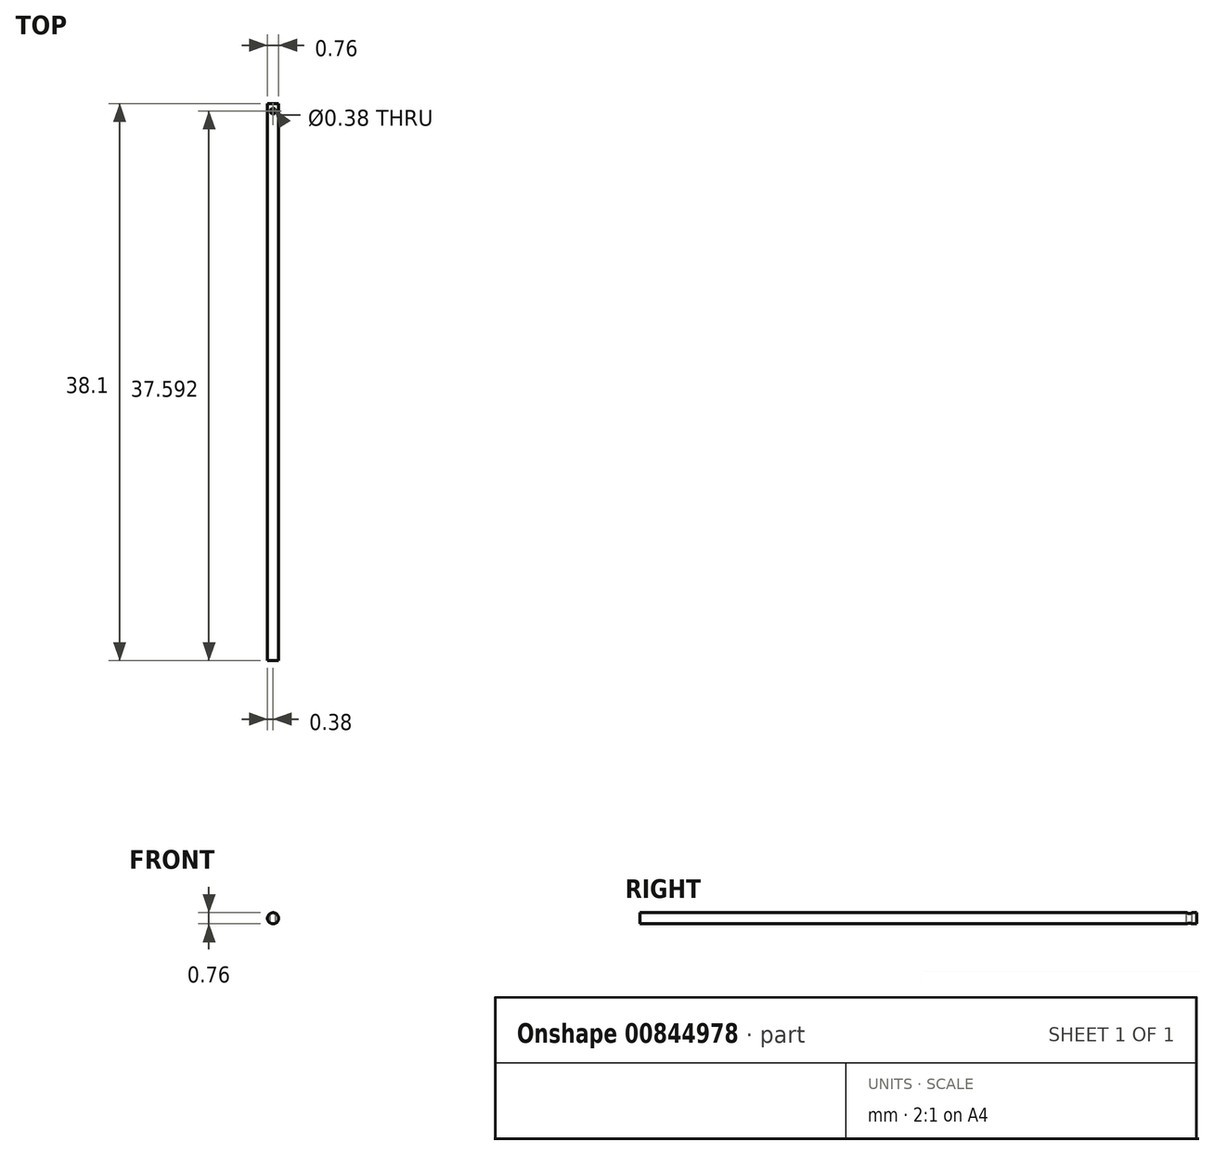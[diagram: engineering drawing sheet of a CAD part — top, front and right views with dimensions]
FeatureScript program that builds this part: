
annotation { "Feature Type Name" : "Feature", "Feature Type Description" : "" }
export const myFeature = defineFeature(function(context is Context, id is Id, definition is map)
    precondition{}
    {
        {
            var Q0;
            Q0=qCreatedBy(makeId("Front.planeOp"),FACE);
            var sketch = newSketch(context, id + "F0", { "sketchPlane" : qUnion([Q0])});
            skCircle(sketch, "E0", {"center": v(0, 0) * mm, "radius": 0.38 * mm});
            skSolve(sketch);
        }
        {
            var Q0;
            Q0 = qSketchRegion(id + "F0", true);
            extrude(context, id + "F1", {"entities" : qUnion([Q0]), "oppositeDirection" : true, "depth" : 38.1 * mm, "offsetDistance" : 25.4 * mm});
        }
        {
            var Q0;
            Q0=qCreatedBy(makeId("Top.planeOp"),FACE);
            cPlane(context, id + "F2", {"entities" : qUnion([Q0]), "cplaneType" : CPlaneType.OFFSET, "offset" : 0.76 * mm, "width" : 152.4 * mm, "height" : 152.4 * mm});
        }
        {
            var Q0;
            Q0=qCreatedBy(id+"F2.planeOp",FACE);
            var sketch = newSketch(context, id + "F3", { "sketchPlane" : qUnion([Q0])});
            skCircle(sketch, "E1", {"center": v(0, 37.6) * mm, "radius": 0.2 * mm});
            skSolve(sketch);
        }
        {
            var Q0;
            Q0 = qSketchRegion(id + "F3", true);
            extrude(context, id + "F4", {"entities" : qUnion([Q0]), "operationType" : NewBodyOperationType.REMOVE, "oppositeDirection" : true, "depth" : 25.4 * mm, "offsetDistance" : 25.4 * mm});
        }
    });
